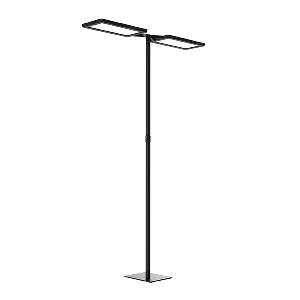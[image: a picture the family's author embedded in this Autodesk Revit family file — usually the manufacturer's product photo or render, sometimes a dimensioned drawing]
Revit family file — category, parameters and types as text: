
# Revit family: yara_doublet_-_yts_2_15000_vtl_r_sw_cee_s0_c_114268000-00808494_c213
name_source: partatom
category: Lighting Fixtures
units: mm (PartAtom-declared; Revit-internal decimal feet)

## family parameters
Cut with Voids When Loaded = No
Host = Face
Light Source = No
Part Type = Normal
Room Calculation Point = No
Round Connector Dimension = Use Diameter
Shared = No

## types (1)
- YARA.doubleT - YTS 2/15000/VTL/R/SW/CEE/S0/C (1 x LED, 15000 lm, VTL)
    Apparent Load = 214 VA
    Approval mark = CE
    CIE Flux Codes = 58 87 97 13 100
    Color Rendering = 80-89
    Color Temperature = VTL
    Control Gear = Electronic ballast
    Default Elevation = 1800 mm
    Description = YTS 2/15000/VTL/R/SW/CEE/S0/R|Free-standing luminaire|light source: LED|work equipment: Electronic ballast DALI|connected load: 220-240 V, 50/60 Hz|Power consumption: approx. 210 W|power factor: approx. 0,966|luminous flux: 30000 lm|luminous efficacy: 142 lm/W|light distribution: Direct/indirect|direct ratio: approx. 13 %|colour temperature: Daylight, ca. 2700-6500 K|color rendering index (CRI): >= 80|chromaticity tolerance:  3 SDCM|technology: Presence and daylight sensor control (PIR)|operation: Wireless switch|luminaire body|material: Aluminium/plastic|surface: Powder coatet|colour: Black|lamp cover: Acrylic (PMMA), Satine, Structured|tubular section|material: Steel tube|surface: Powder-coated|Form: Tubular section upright|colour of tubular section: Black|luminaire base|Form: Rectangular flat|weight (net): approx. 24.0 kg|mains lead: 3.00 m Mains plug CEE 7/VII|Fastening: Floor standing base|glare control: Conical prismatic screen|luminance(L65): <= 2700 cd/m|unified glare rating(4H 8H): <=  16|special features: App control, Asymmetric radiation, Biodynamic light VTL, Direct and indirect lighting component with edge light and light guidetechnology for a homogeneous light exit, Flicker-free, Magnetic control panel, freely positionable, PIR movement and daylight sensor, TALK Bluetooth|Approval mark: VDE - ENEC|
    Frequency = 50 Hz, 60 Hz
    Height = 24 mm  [stored 0.0787402 ft]
    Lamp = 1 x LED
    Lamp Light Flux = 15000 lm
    Lamp count = 1
    Length = 690 mm
    Luminous efficacy = 140 lm/W
    Manufacturer = Waldmann
    ModVariant = No
    Model = 114268000-00808494
    Mounting Place = Floor
    Mounting Type = Freestanding
    Number of Poles = 1
    OnlyDefault = Yes
    Power Factor = 1
    Product Name = YARA.doubleT - YTS 2/15000/VTL/R/SW/CEE/S0/C
    Product group = Free standing luminaire
    ProductGroupID = 13
    Protection Class = Protection class I
    Protection Degree = IP 20
    RLX_Detail_Level = 1
    RlxData = <blob elided: 64557 chars, md5=13eb0cb9>
    Socket = socket
    Standby Power = 0 W
    System Light Flux = 30000 lm
    System Power = 214 W
    Type Comments = Product without accessories
    Type Image = yts-r-sw-r.jpg
    URL = http://relux.com
    VarID = ---
    Voltage = 230 V
    Voltage Range = 220-240 V
    Weight = 0.00 kg
    Width = 358 mm

note: [stored X ft] marks values corroborated as IEEE doubles in the binary element streams (Revit-internal decimal feet)

## geometry (parser evidence)
native form markers: Blend x4, Sweep x20
no freeform markers — native parametric forms only
